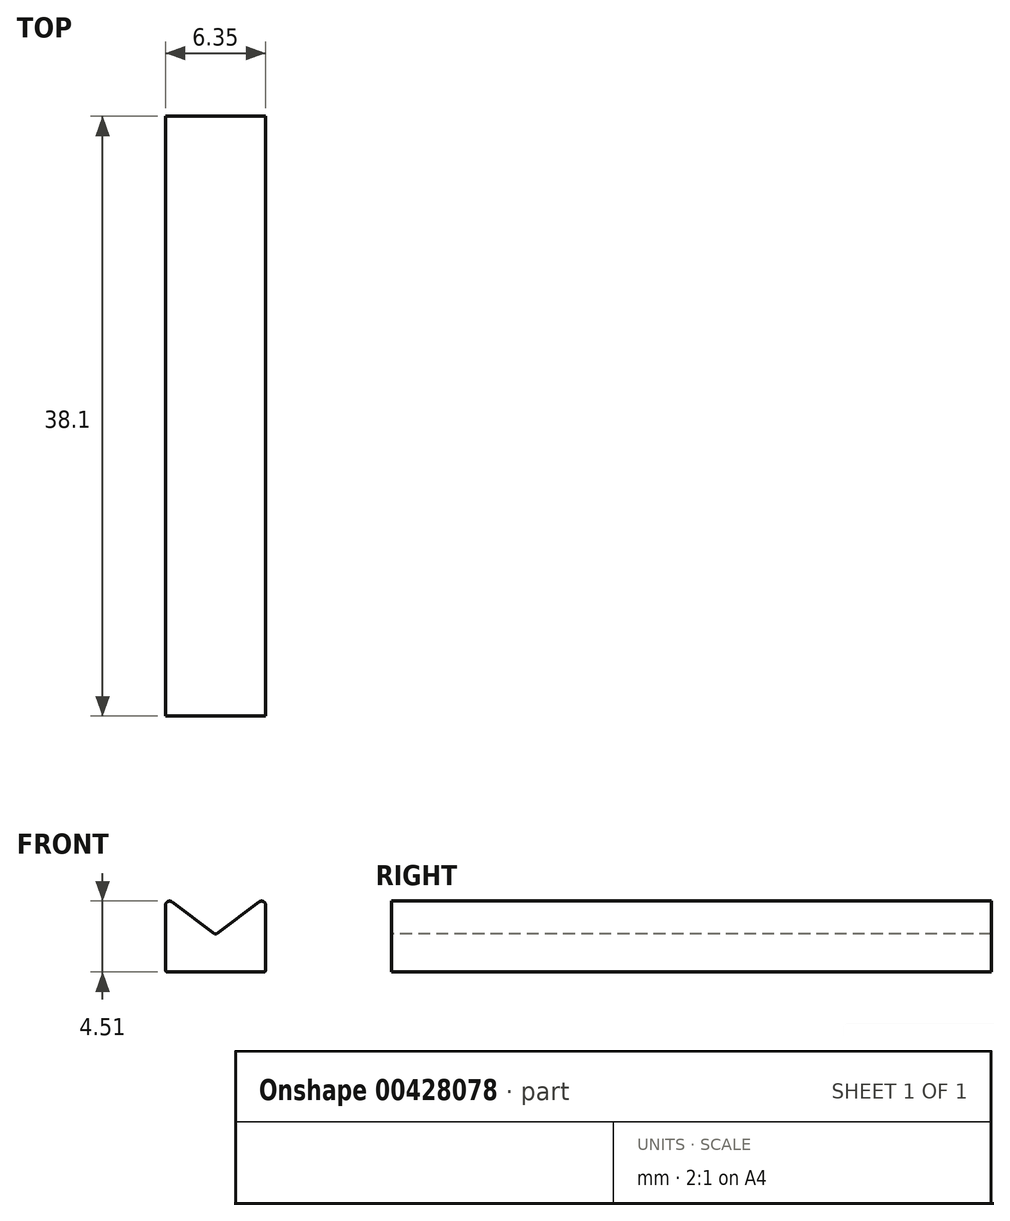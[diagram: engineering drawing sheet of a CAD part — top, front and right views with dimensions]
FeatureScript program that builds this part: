
annotation { "Feature Type Name" : "Feature", "Feature Type Description" : "" }
export const myFeature = defineFeature(function(context is Context, id is Id, definition is map)
    precondition{}
    {
        {
            var Q0;
            Q0=qCreatedBy(makeId("Front.planeOp"),FACE);
            var sketch = newSketch(context, id + "F0", { "sketchPlane" : qUnion([Q0])});
            skLineSegment(sketch, "E0.bottom", {"start": v(0, 0) * mm, "end": v(6.35, 0) * mm});
            skLineSegment(sketch, "E0.top", {"start": v(0, -4.76) * mm, "end": v(6.35, -4.76) * mm});
            skLineSegment(sketch, "E0.left", {"start": v(0, 0) * mm, "end": v(0, -4.76) * mm});
            skLineSegment(sketch, "E0.right", {"start": v(6.35, 0) * mm, "end": v(6.35, -4.76) * mm});
            skLineSegment(sketch, "E1", {"start": v(0, -4.76) * mm, "end": v(0, -2.38) * mm});
            skLineSegment(sketch, "E2", {"start": v(6.35, -2.38) * mm, "end": v(0, -2.38) * mm});
            skLineSegment(sketch, "E3", {"start": v(0, 0) * mm, "end": v(3.17, -2.38) * mm});
            skLineSegment(sketch, "E4", {"start": v(3.18, -2.38) * mm, "end": v(6.35, 0) * mm});
            skSolve(sketch);
        }
        {
            var Q0;
            {var subQ2=sQuery(id+"F0.wireOp",EDGE,"E0.top");Q0=makeQuery(id+"F0.imprint","IMPRINT",FACE,{"disambiguationData":[TD([[makeQuery(id+"F0.imprint","IMPRINT",EDGE,{"derivedFrom":subQ2}),1.0]])]});}
            var Q1;
            {var subQ0=sQuery(id+"F0.wireOp",EDGE,"E0.left");Q1=makeQuery(id+"F0.imprint","IMPRINT",FACE,{"disambiguationData":[TD([[makeQuery(id+"F0.imprint","IMPRINT",EDGE,{"derivedFrom":subQ0}),1.0]])]});}
            var Q2;
            {var subQ0=sQuery(id+"F0.wireOp",EDGE,"E4");Q2=makeQuery(id+"F0.imprint","IMPRINT",FACE,{"disambiguationData":[TD([[makeQuery(id+"F0.imprint","IMPRINT",EDGE,{"derivedFrom":subQ0}),-1.0]])]});}
            extrude(context, id + "F1", {"entities" : qUnion([Q0, Q1, Q2]), "depth" : 38.1 * mm});
        }
        {
            var Q0;
            Q0=makeQuery(id+"F1.opExtrude","SWEPT_EDGE",EDGE,{"disambiguationData":[OSD([sQuery(id+"F0.wireOp",EDGE,"E0.bottom"),sQuery(id+"F0.wireOp",EDGE,"E0.left"),sQuery(id+"F0.wireOp",EDGE,"E3")])]});
            var Q1;
            Q1=makeQuery(id+"F1.opExtrude","SWEPT_EDGE",EDGE,{"disambiguationData":[OSD([sQuery(id+"F0.wireOp",EDGE,"E0.bottom"),sQuery(id+"F0.wireOp",EDGE,"E0.right"),sQuery(id+"F0.wireOp",EDGE,"E4")])]});
            fillet(context, id + "F2", {"entities" : qUnion([Q0, Q1]), "radius" : 0.25 * mm, "allowEdgeOverflow" : false});
        }
        {
            var Q0;
            Q0=makeQuery(id+"F1.opExtrude","SWEPT_EDGE",EDGE,{"disambiguationData":[OSD([sQuery(id+"F0.wireOp",EDGE,"E2"),sQuery(id+"F0.wireOp",EDGE,"E3"),sQuery(id+"F0.wireOp",EDGE,"E4")])]});
            var Q1;
            Q1=makeQuery(id+"F1.opExtrude","SWEPT_EDGE",EDGE,{"disambiguationData":[OSD([sQuery(id+"F0.wireOp",EDGE,"E0.top"),sQuery(id+"F0.wireOp",EDGE,"E0.right")])]});
            var Q2;
            Q2=makeQuery(id+"F1.opExtrude","SWEPT_EDGE",EDGE,{"disambiguationData":[OSD([sQuery(id+"F0.wireOp",EDGE,"E0.top"),sQuery(id+"F0.wireOp",EDGE,"E1")])]});
            fillet(context, id + "F3", {"entities" : qUnion([Q0, Q1, Q2]), "radius" : 0.13 * mm, "allowEdgeOverflow" : false});
        }
        {
            var Q0;
            Q0=makeQuery(id+"F1.opExtrude","SWEPT_FACE",FACE,{"disambiguationData":[OSD([sQuery(id+"F0.wireOp",EDGE,"E4")])]});
            var sketch = newSketch(context, id + "F4", { "sketchPlane" : qUnion([Q0])});
            skLineSegment(sketch, "E5", {"start": v(4.57, -38.1) * mm, "end": v(3.68, -38.1) * mm});
            skLineSegment(sketch, "E6", {"start": v(3.68, -38.1) * mm, "end": v(3.68, 0) * mm});
            skLineSegment(sketch, "E7", {"start": v(3.68, -38.1) * mm, "end": v(3.68, -19.05) * mm});
            skSolve(sketch);
        }
    });
